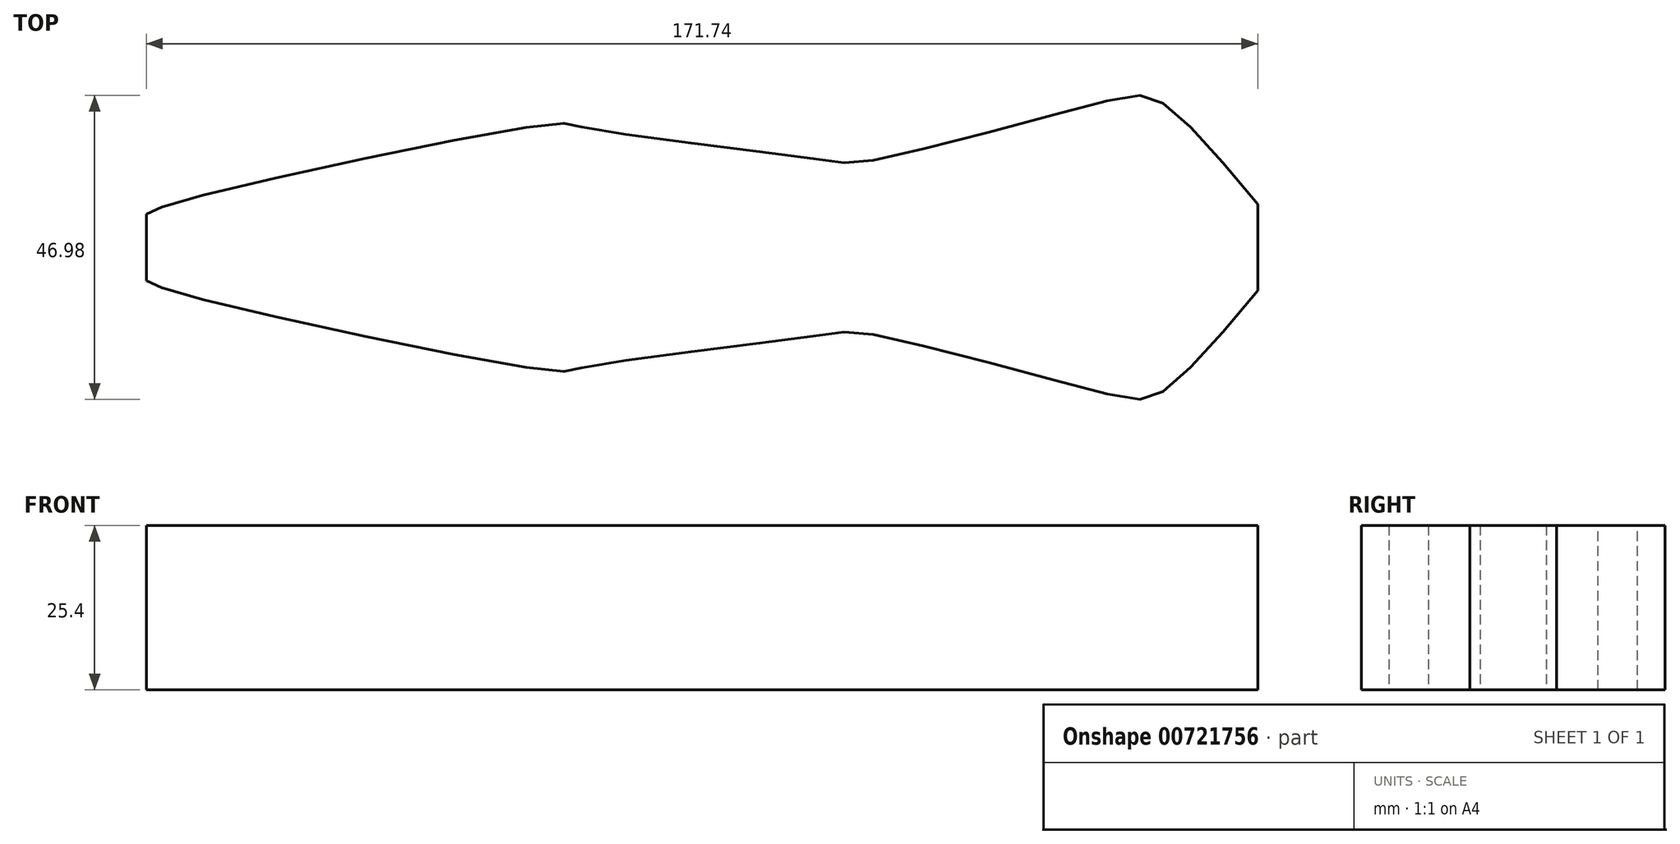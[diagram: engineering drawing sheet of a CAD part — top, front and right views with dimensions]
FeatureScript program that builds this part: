
annotation { "Feature Type Name" : "Feature", "Feature Type Description" : "" }
export const myFeature = defineFeature(function(context is Context, id is Id, definition is map)
    precondition{}
    {
        {
            var Q0;
            Q0=qCreatedBy(makeId("Top.planeOp"),FACE);
            var sketch = newSketch(context, id + "F0", { "sketchPlane" : qUnion([Q0])});
            skFitSpline(sketch, "E0", {"points": [v(-77.57, 5.12) * mm, v(-72.5, 7.08) * mm, v(-14.5, 19.15) * mm, v(-10.28, 18.58) * mm, v(25.2, 13.77) * mm, v(34.77, 13.49) * mm, v(71.36, 22.75) * mm, v(79.25, 22.47) * mm, v(94.17, 6.7) * mm], "startDerivative": vector(38.04, 22.54) * mm, "endDerivative": vector(124.74, -150.37) * mm});
            skFitSpline(sketch, "E1.MirrorCS", {"points": [v(-77.57, -5.12) * mm, v(-72.5, -7.08) * mm, v(-14.5, -19.15) * mm, v(-10.28, -18.58) * mm, v(25.2, -13.77) * mm, v(34.77, -13.49) * mm, v(71.36, -22.75) * mm, v(79.25, -22.47) * mm, v(94.17, -6.7) * mm], "startDerivative": vector(38.04, -22.54) * mm, "endDerivative": vector(124.74, 150.37) * mm});
            skLineSegment(sketch, "E2", {"start": v(-77.57, 5.12) * mm, "end": v(-77.57, -5.12) * mm});
            skLineSegment(sketch, "E3", {"start": v(94.17, 6.7) * mm, "end": v(94.17, -6.7) * mm});
            skSolve(sketch);
        }
        {
            var Q0;
            Q0=makeQuery(id+"F0.imprint","IMPRINT",FACE,{"disambiguationData":[TD([[makeQuery(id+"F0.imprint","IMPRINT",EDGE,{"derivedFrom":sQuery(id+"F0.wireOp",EDGE,"E0")}),-1.0]])]});
            extrude(context, id + "F1", {"entities" : qUnion([Q0]), "depth" : 25.4 * mm, "offsetDistance" : 25.4 * mm});
        }
    });
